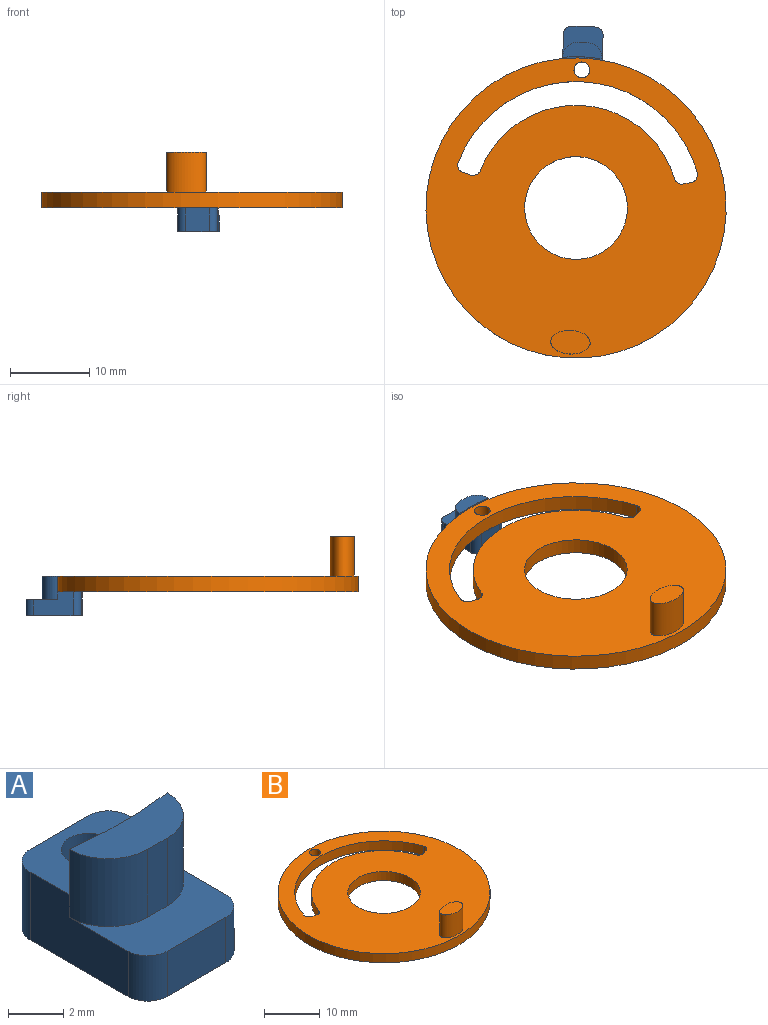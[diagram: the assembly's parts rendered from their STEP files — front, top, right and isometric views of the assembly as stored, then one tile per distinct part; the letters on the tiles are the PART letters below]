
ASSEMBLY  parts=2 mates=1
PART A: 17 faces, bbox 5x7x5 mm
  f0: plane 5x3mm, normal (1,0,0), area 12mm2, adj f5,f6,f9,f11,f13,f16
  f1: plane 3x2mm, normal (0,-1,0), area 6mm2, adj f6,f11,f15,f16
  f2: plane 5x2mm, normal (0,0,1), area 7.7mm2, adj f7,f12,f13,f14
  f3: plane 5x3mm, normal (-1,0,0), area 12mm2, adj f5,f6,f10,f11,f14,f15
  f4: plane 3x3mm, normal (0,1,0), area 9mm2, adj f5,f6,f9,f10
  f5: plane 5x3.22mm, normal (0,0,1), area 12mm2, adj f0,f3,f4,f7,f8,f9,f10
  f6: plane 7x5mm, normal (0,0,-1), area 31mm2, adj f0,f1,f3,f4,f8,f9,f10,f15
  f7: extruded ~5x2mm, area 10mm2, adj f2,f5,f13,f14
  f8: cylinder r=1mm len=3mm, axis (0,0,-1), area 18.8mm2, adj f5,f6
  f9: cylinder r=1mm len=3mm, axis (0,0,-1), area 4.7mm2, adj f0,f4,f5,f6
  f10: cylinder r=1mm len=3mm, axis (0,0,-1), area 4.7mm2, adj f3,f4,f5,f6
  f11: plane 5x4mm, normal (0,0,1), area 11.3mm2, adj f0,f1,f3,f12,f13,f14,f15,f16
  f12: plane 3x1mm, normal (0,-1,0), area 3mm2, adj f2,f11,f13,f14
  f13: cylinder r=2mm len=3mm, axis (0,0,-1), area 9.4mm2, adj f0,f2,f7,f11,f12
  f14: cylinder r=2mm len=3mm, axis (0,0,-1), area 9.4mm2, adj f2,f3,f7,f11,f12
  f15: cylinder r=1mm len=2mm, axis (0,0,1), area 3.1mm2, adj f1,f3,f6,f11
  f16: cylinder r=1mm len=2mm, axis (0,0,1), area 3.1mm2, adj f0,f1,f6,f11
PART B: 15 faces, bbox 38x38x7 mm
  f0: plane 38x38mm, normal (0,0,-1), area 885.2mm2, adj f2,f3,f4,f7,f8,f9,f10,f11
  f1: plane 38x38mm, normal (0,0,1), area 873.4mm2, adj f2,f3,f4,f5,f7,f8,f9,f10
  f2: cylinder r=1mm len=2mm, axis (0,0,1), area 12.6mm2, adj f0,f1
  f3: cylinder r=19mm len=38mm, axis (0,0,1), area 238.8mm2, adj f0,f1
  f4: cylinder r=6.5mm len=13mm, axis (0,0,1), area 81.7mm2, adj f0,f1
  f5: extruded ~5x5mm, area 63.8mm2, adj f1,f6
  f6: plane 5x3mm, normal (0,0,1), area 11.8mm2, adj f5
  f7: cylinder r=13mm len=24.57mm, axis (0,0,1), area 64.4mm2, adj f0,f1,f11,f14
  f8: plane 2x0.97mm, normal (-0.26,0.97,0), area 2mm2, adj f0,f1,f11,f12
  f9: cylinder r=16mm len=30.29mm, axis (0,0,1), area 79.5mm2, adj f0,f1,f12,f13
  f10: plane 2x0.97mm, normal (0.26,0.97,0), area 2mm2, adj f0,f1,f13,f14
  f11: cylinder r=1mm len=2mm, axis (0,0,1), area 3mm2, adj f0,f1,f7,f8
  f12: cylinder r=1mm len=2mm, axis (0,0,1), area 3.3mm2, adj f0,f1,f8,f9
  f13: cylinder r=1mm len=2mm, axis (0,0,1), area 3.3mm2, adj f0,f1,f9,f10
  f14: cylinder r=1mm len=2mm, axis (0,0,1), area 3mm2, adj f0,f1,f7,f10
PLACE A rot(axis=(0,0,1),177.6deg) t=(-32.33,-57.43,-2.98)mm
PLACE B rot(axis=(0,0,-1),2.4deg) t=(0.78,-64.34,2.02)mm
MATE parallel A.f8 <-> B.f2  axis (0,0,1) through (-16.72,-15.82,0.02)mm
